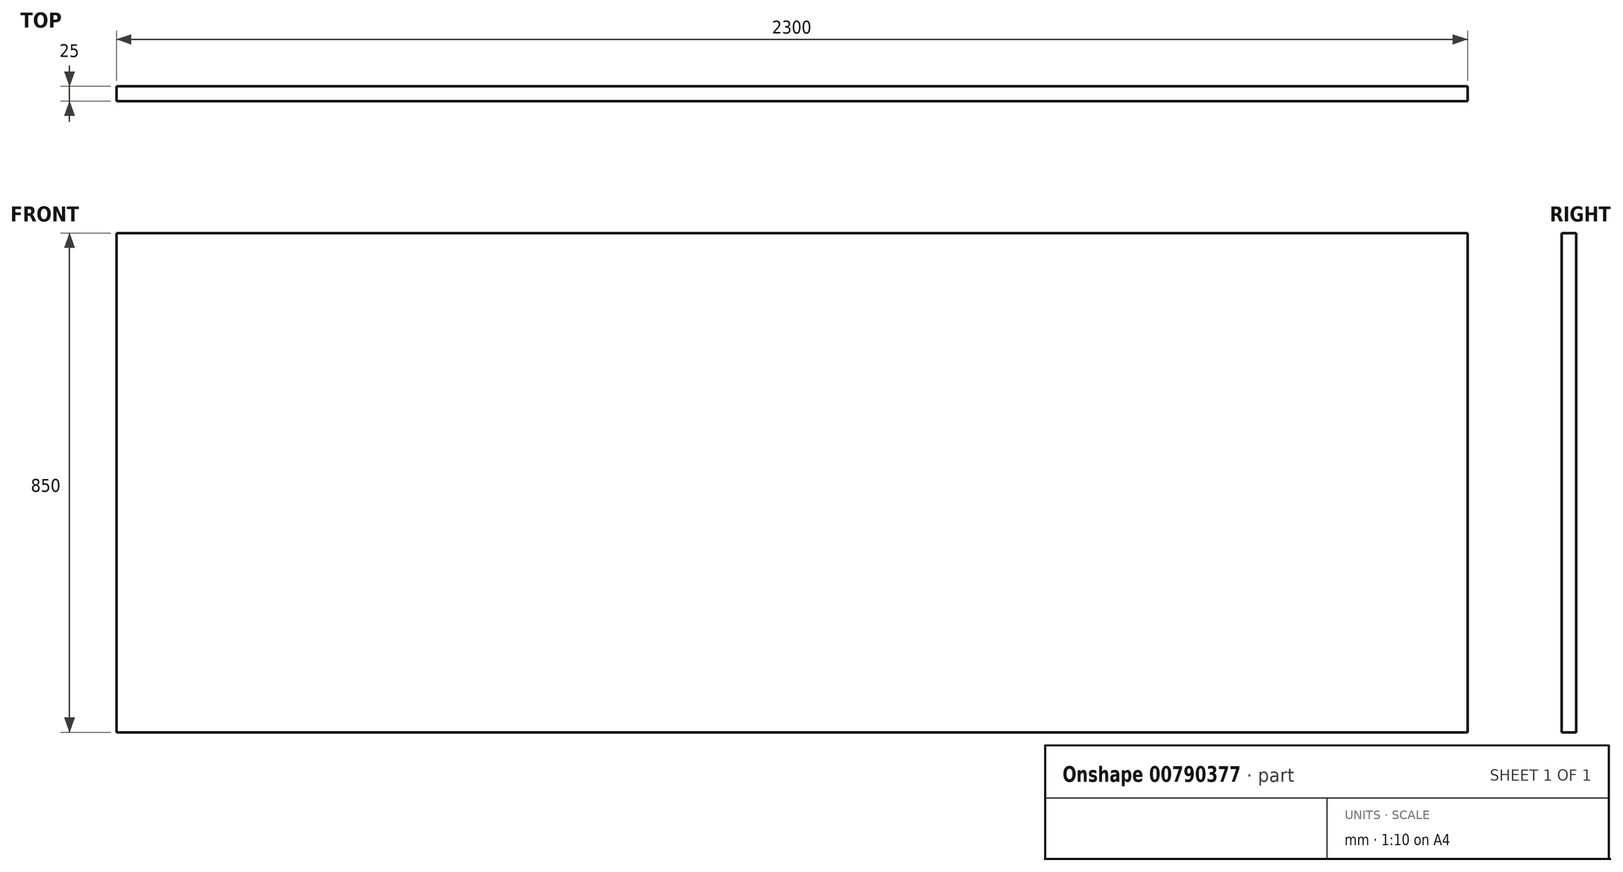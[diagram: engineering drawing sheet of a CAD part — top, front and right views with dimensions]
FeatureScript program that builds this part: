
annotation { "Feature Type Name" : "Feature", "Feature Type Description" : "" }
export const myFeature = defineFeature(function(context is Context, id is Id, definition is map)
    precondition{}
    {
        {
            var Q0;
            Q0=qCreatedBy(makeId("Front.planeOp"),FACE);
            var sketch = newSketch(context, id + "F0", { "sketchPlane" : qUnion([Q0])});
            skLineSegment(sketch, "E0", {"start": v(-384.15, 70) * mm, "end": v(1115.85, 70) * mm});
            skLineSegment(sketch, "E1", {"start": v(1115.85, 70) * mm, "end": v(1115.85, -780) * mm});
            skLineSegment(sketch, "E2", {"start": v(-384.15, 70) * mm, "end": v(-384.15, -780) * mm});
            skLineSegment(sketch, "E3", {"start": v(-384.15, -780) * mm, "end": v(1115.85, -780) * mm});
            skLineSegment(sketch, "E4", {"start": v(1115.85, 70) * mm, "end": v(1515.85, 70) * mm});
            skLineSegment(sketch, "E5", {"start": v(1515.85, -780) * mm, "end": v(1115.85, -780) * mm});
            skLineSegment(sketch, "E6", {"start": v(-384.15, 70) * mm, "end": v(-784.15, 70) * mm});
            skLineSegment(sketch, "E7", {"start": v(-784.15, 70) * mm, "end": v(-784.15, -780) * mm});
            skLineSegment(sketch, "E8", {"start": v(1515.85, 70) * mm, "end": v(1515.85, -780) * mm});
            skLineSegment(sketch, "E9", {"start": v(-784.15, -780) * mm, "end": v(-384.15, -780) * mm});
            skSolve(sketch);
        }
        {
            var Q0;
            Q0 = qSketchRegion(id + "F0", true);
            extrude(context, id + "F1", {"entities" : qUnion([Q0]), "oppositeDirection" : true, "depth" : 25 * mm, "offsetDistance" : 25 * mm});
        }
    });
